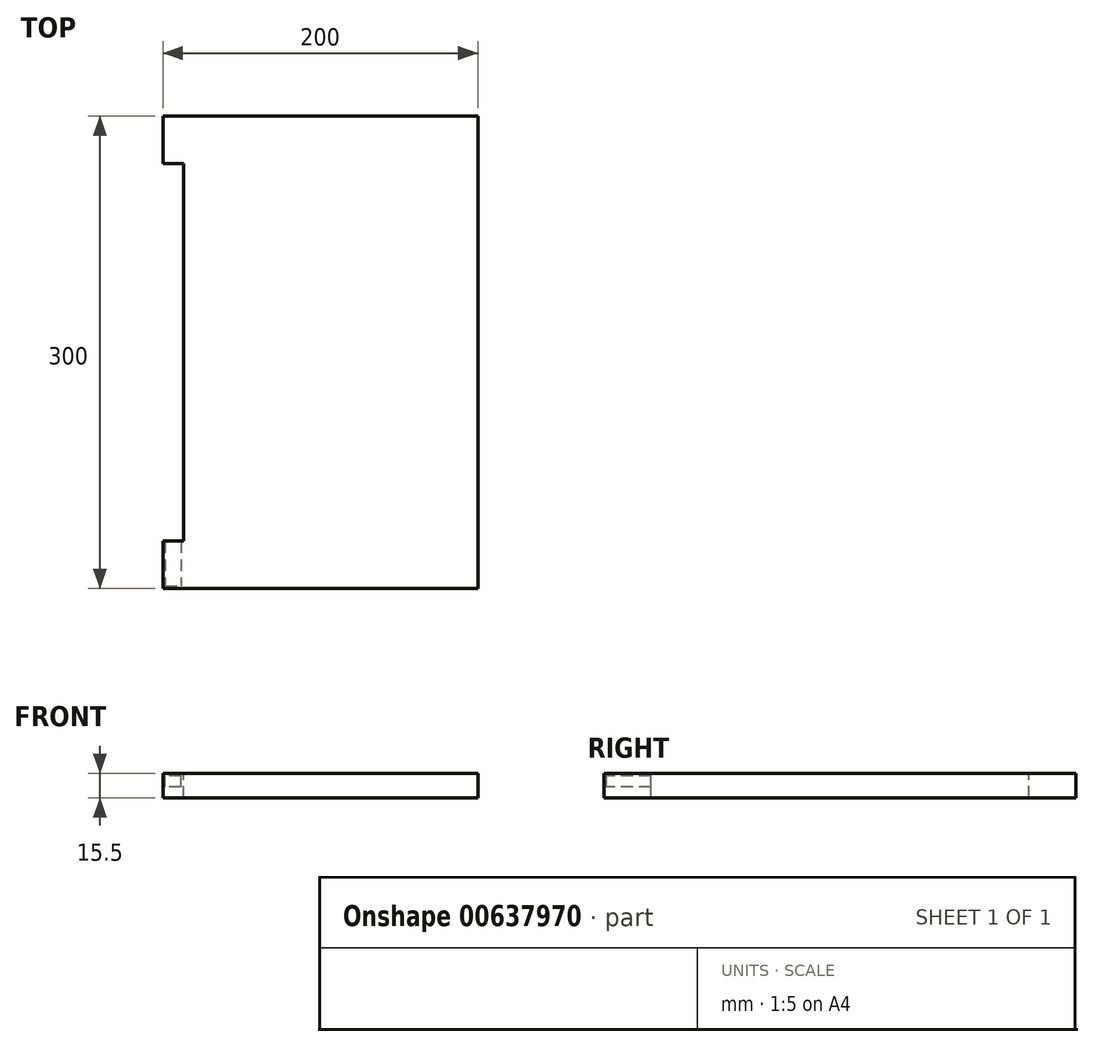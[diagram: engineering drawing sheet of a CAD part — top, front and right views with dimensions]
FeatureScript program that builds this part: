
annotation { "Feature Type Name" : "Feature", "Feature Type Description" : "" }
export const myFeature = defineFeature(function(context is Context, id is Id, definition is map)
    precondition{}
    {
        {
            var Q0;
            Q0=qCreatedBy(makeId("Front.planeOp"),FACE);
            var sketch = newSketch(context, id + "F0", { "sketchPlane" : qUnion([Q0])});
            skLineSegment(sketch, "E0.bottom", {"start": v(0, 0) * mm, "end": v(200, 0) * mm});
            skLineSegment(sketch, "E0.top", {"start": v(0, 15.5) * mm, "end": v(200, 15.5) * mm});
            skLineSegment(sketch, "E0.left", {"start": v(0, 0) * mm, "end": v(0, 15.5) * mm});
            skLineSegment(sketch, "E0.right", {"start": v(200, 0) * mm, "end": v(200, 15.5) * mm});
            skSolve(sketch);
        }
        {
            var Q0;
            Q0=makeQuery(id+"F0.imprint","IMPRINT",FACE,{"disambiguationData":[TD([[makeQuery(id+"F0.imprint","IMPRINT",EDGE,{"derivedFrom":sQuery(id+"F0.wireOp",EDGE,"E0.bottom")}),1.0]])]});
            extrude(context, id + "F1", {"entities" : qUnion([Q0]), "oppositeDirection" : true, "depth" : 300 * mm, "offsetDistance" : 25 * mm});
        }
        {
            var Q0;
            Q0=makeQuery(id+"F1.opExtrude","SWEPT_FACE",FACE,{"disambiguationData":[OSD([sQuery(id+"F0.wireOp",EDGE,"E0.top")])]});
            var sketch = newSketch(context, id + "F2", { "sketchPlane" : qUnion([Q0])});
            skLineSegment(sketch, "E1.bottom", {"start": v(0, 150) * mm, "end": v(13, 150) * mm});
            skLineSegment(sketch, "E1.top", {"start": v(0, 270) * mm, "end": v(13, 270) * mm});
            skLineSegment(sketch, "E1.left", {"start": v(0, 150) * mm, "end": v(0, 270) * mm});
            skLineSegment(sketch, "E1.right", {"start": v(13, 150) * mm, "end": v(13, 270) * mm});
            skLineSegment(sketch, "E2.top", {"start": v(0, 30) * mm, "end": v(13, 30) * mm});
            skLineSegment(sketch, "E2.left", {"start": v(0, 150) * mm, "end": v(0, 30) * mm});
            skLineSegment(sketch, "E2.right", {"start": v(13, 150) * mm, "end": v(13, 30) * mm});
            skSolve(sketch);
        }
        {
            var Q0;
            Q0 = qSketchRegion(id + "F2", true);
            extrude(context, id + "F3", {"entities" : qUnion([Q0]), "operationType" : NewBodyOperationType.REMOVE, "endBound" : BoundingType.THROUGH_ALL, "oppositeDirection" : true, "depth" : 25 * mm, "offsetDistance" : 25 * mm});
        }
        {
            var Q0;
            Q0=makeQuery(id+"F1.opExtrude","CAP_FACE",FACE,{"disambiguationData":[OSD([sQuery(id+"F0.wireOp",EDGE,"E0.bottom"),sQuery(id+"F0.wireOp",EDGE,"E0.top"),sQuery(id+"F0.wireOp",EDGE,"E0.left"),sQuery(id+"F0.wireOp",EDGE,"E0.right")])],"isStart":true});
            cPlane(context, id + "F4", {"entities" : qUnion([Q0]), "cplaneType" : CPlaneType.OFFSET, "offset" : 1.5 * mm, "oppositeDirection" : true, "width" : 150 * mm, "height" : 150 * mm});
        }
        {
            var Q0;
            Q0=qCreatedBy(id+"F4.planeOp",FACE);
            var sketch = newSketch(context, id + "F5", { "sketchPlane" : qUnion([Q0])});
            skLineSegment(sketch, "E3", {"start": v(0, 15.5) * mm, "end": v(1.5, 15.5) * mm, "construction": true});
            skLineSegment(sketch, "E4", {"start": v(1.5, 15.5) * mm, "end": v(1.5, 14) * mm, "construction": true});
            skLineSegment(sketch, "E5.bottom", {"start": v(1.5, 14) * mm, "end": v(11.5, 14) * mm});
            skLineSegment(sketch, "E5.top", {"start": v(1.5, 7) * mm, "end": v(11.5, 7) * mm});
            skLineSegment(sketch, "E5.left", {"start": v(1.5, 14) * mm, "end": v(1.5, 7) * mm});
            skLineSegment(sketch, "E5.right", {"start": v(11.5, 14) * mm, "end": v(11.5, 7) * mm});
            skSolve(sketch);
        }
        {
            var Q0;
            Q0 = qSketchRegion(id + "F5", true);
            extrude(context, id + "F6", {"entities" : qUnion([Q0]), "operationType" : NewBodyOperationType.REMOVE, "endBound" : BoundingType.UP_TO_NEXT, "oppositeDirection" : true, "depth" : 27 * mm, "offsetDistance" : 25 * mm});
        }
    });
